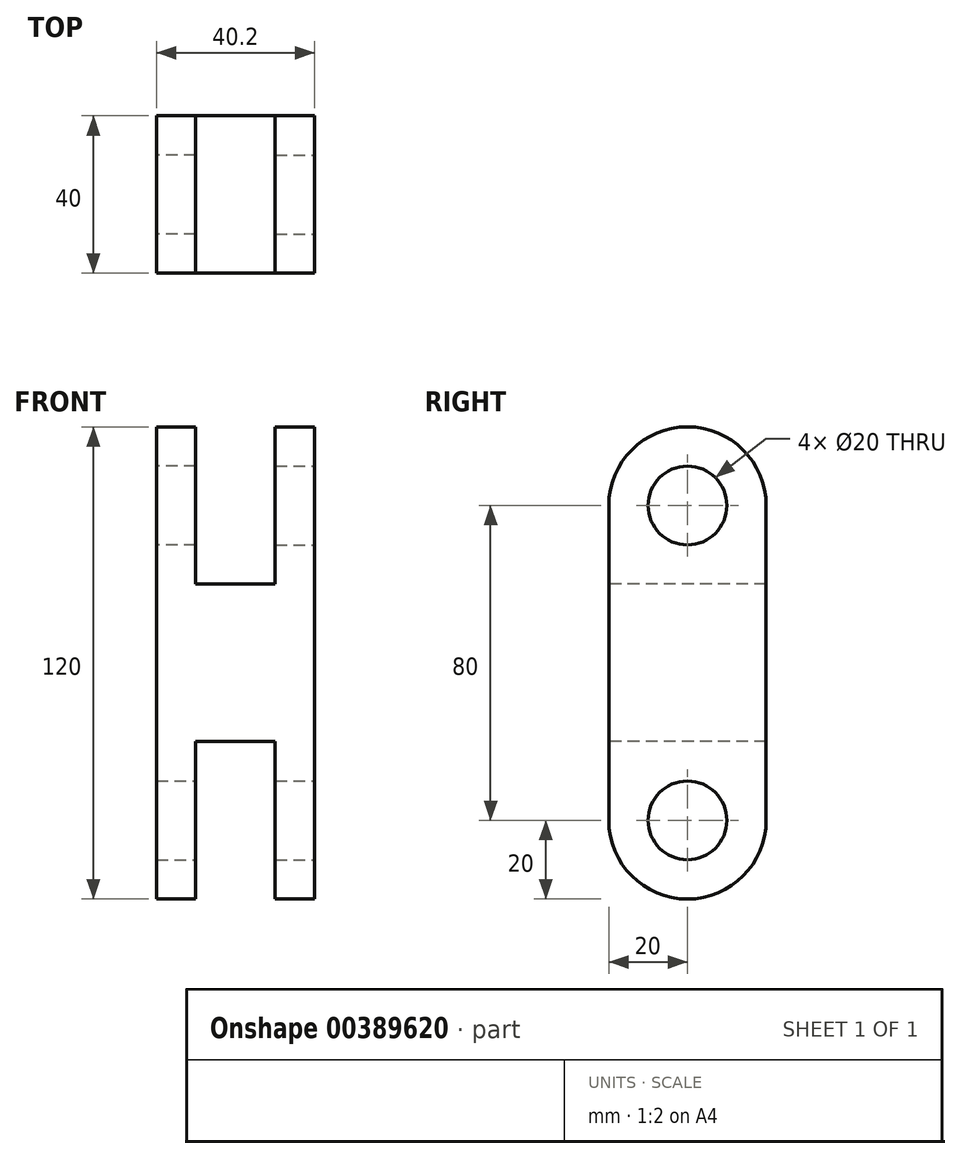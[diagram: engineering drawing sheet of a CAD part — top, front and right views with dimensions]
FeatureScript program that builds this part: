
annotation { "Feature Type Name" : "Feature", "Feature Type Description" : "" }
export const myFeature = defineFeature(function(context is Context, id is Id, definition is map)
    precondition{}
    {
        {
            var Q0;
            Q0=qCreatedBy(makeId("Right.planeOp"),FACE);
            var sketch = newSketch(context, id + "F0", { "sketchPlane" : qUnion([Q0])});
            skLineSegment(sketch, "E0.bottom", {"start": v(20, 40) * mm, "end": v(-20, 40) * mm});
            skLineSegment(sketch, "E0.top", {"start": v(20, -40) * mm, "end": v(-20, -40) * mm});
            skLineSegment(sketch, "E0.left", {"start": v(20, 40) * mm, "end": v(20, -40) * mm});
            skLineSegment(sketch, "E0.right", {"start": v(-20, 40) * mm, "end": v(-20, -40) * mm});
            skPoint(sketch, "E0.middle", {"position": v(0, 0) * mm});
            skSolve(sketch);
        }
        {
            var Q0;
            Q0 = qSketchRegion(id + "F0", true);
            extrude(context, id + "F1", {"entities" : qUnion([Q0]), "depth" : 20.1 * mm});
        }
        {
            var Q0;
            Q0=makeQuery(id+"F1.opExtrude","CAP_FACE",FACE,{"disambiguationData":[OSD([sQuery(id+"F0.wireOp",EDGE,"E0.bottom"),sQuery(id+"F0.wireOp",EDGE,"E0.top"),sQuery(id+"F0.wireOp",EDGE,"E0.left"),sQuery(id+"F0.wireOp",EDGE,"E0.right")])],"isStart":false});
            var sketch = newSketch(context, id + "F2", { "sketchPlane" : qUnion([Q0])});
            skSolve(sketch);
        }
        {
            var Q0;
            Q0=makeQuery(id+"F2.imprint","IMPRINT",FACE,{"disambiguationData":[TD([[makeQuery(id+"F2.imprint","IMPRINT",EDGE,{"derivedFrom":makeQuery(id+"F1.opExtrude","CAP_EDGE",EDGE,{"disambiguationData":[OSD([sQuery(id+"F0.wireOp",EDGE,"E0.bottom")])],"isStart":false})}),1.0]])]});
            var sketch = newSketch(context, id + "F3", { "sketchPlane" : qUnion([Q0])});
            skLineSegment(sketch, "E1.bottom", {"start": v(-20, 40) * mm, "end": v(20, 40) * mm});
            skLineSegment(sketch, "E1.left", {"start": v(-20, 40) * mm, "end": v(-20, 60) * mm});
            skLineSegment(sketch, "E1.right", {"start": v(20, 40) * mm, "end": v(20, 60) * mm});
            skArc(sketch, "E2", {"start": v(20, 60) * mm, "mid": v(0, 80) * mm, "end": v(-20, 60) * mm});
            skCircle(sketch, "E3", {"center": v(0, 60) * mm, "radius": 10 * mm});
            skSolve(sketch);
        }
        {
            var Q0;
            Q0 = qSketchRegion(id + "F3", true);
            extrude(context, id + "F4", {"entities" : qUnion([Q0]), "operationType" : NewBodyOperationType.ADD, "oppositeDirection" : true, "depth" : 10 * mm});
        }
        {
            var Q0;
            Q0=makeQuery(id+"F1.opExtrude","SWEPT_BODY",BODY,{"disambiguationData":[OSD([sQuery(id+"F0.wireOp",EDGE,"E0.bottom"),sQuery(id+"F0.wireOp",EDGE,"E0.top"),sQuery(id+"F0.wireOp",EDGE,"E0.left"),sQuery(id+"F0.wireOp",EDGE,"E0.right")])]});
            var Q1;
            Q1=qCreatedBy(makeId("Right.planeOp"),FACE);
            mirror(context, id + "F5", {"operationType" : NewBodyOperationType.ADD, "entities" : qUnion([Q0]), "mirrorPlane" : qUnion([Q1])});
        }
        {
            var Q0;
            {var subQ0=makeQuery(id+"F4.boolean.opBoolean","MERGE",FACE,{"derivedFrom":[makeQuery(id+"F1.opExtrude","SWEPT_FACE",FACE,{"disambiguationData":[OSD([sQuery(id+"F0.wireOp",EDGE,"E0.right")])]}),makeQuery(id+"F4.opExtrude","SWEPT_FACE",FACE,{"disambiguationData":[OSD([sQuery(id+"F3.wireOp",EDGE,"E1.left")])]})]});Q0=makeQuery(id+"F5.boolean.opBoolean","MERGE",FACE,{"derivedFrom":[subQ0,makeQuery(id+"F5.opPattern","COPY",FACE,{"derivedFrom":subQ0,"instanceName":"1"})]});}
            var sketch = newSketch(context, id + "F6", { "sketchPlane" : qUnion([Q0])});
            skLineSegment(sketch, "E4.bottom", {"start": v(-10.1, -40) * mm, "end": v(10.1, -40) * mm});
            skLineSegment(sketch, "E4.top", {"start": v(-10.1, 0) * mm, "end": v(10.1, 0) * mm});
            skLineSegment(sketch, "E4.left", {"start": v(-10.1, -40) * mm, "end": v(-10.1, 0) * mm});
            skLineSegment(sketch, "E4.right", {"start": v(10.1, -40) * mm, "end": v(10.1, 0) * mm});
            skSolve(sketch);
        }
        {
            var Q0;
            Q0 = qSketchRegion(id + "F6", true);
            var Q1;
            {var subQ0=makeQuery(id+"F4.boolean.opBoolean","MERGE",FACE,{"derivedFrom":[makeQuery(id+"F1.opExtrude","SWEPT_FACE",FACE,{"disambiguationData":[OSD([sQuery(id+"F0.wireOp",EDGE,"E0.left")])]}),makeQuery(id+"F4.opExtrude","SWEPT_FACE",FACE,{"disambiguationData":[OSD([sQuery(id+"F3.wireOp",EDGE,"E1.right")])]})]});Q1=makeQuery(id+"F5.boolean.opBoolean","MERGE",FACE,{"derivedFrom":[subQ0,makeQuery(id+"F5.opPattern","COPY",FACE,{"derivedFrom":subQ0,"instanceName":"1"})]});}
            extrude(context, id + "F7", {"entities" : qUnion([Q0]), "operationType" : NewBodyOperationType.REMOVE, "endBound" : BoundingType.UP_TO_SURFACE, "oppositeDirection" : true, "endBoundEntityFace" : qUnion([Q1]), "depth" : 25 * mm});
        }
        {
            var Q0;
            Q0=makeQuery(id+"F2.imprint","IMPRINT",FACE,{"disambiguationData":[TD([[makeQuery(id+"F2.imprint","IMPRINT",EDGE,{"derivedFrom":makeQuery(id+"F1.opExtrude","CAP_EDGE",EDGE,{"disambiguationData":[OSD([sQuery(id+"F0.wireOp",EDGE,"E0.bottom")])],"isStart":false})}),1.0]])]});
            var sketch = newSketch(context, id + "F8", { "sketchPlane" : qUnion([Q0])});
            skLineSegment(sketch, "E5", {"start": v(0, -40) * mm, "end": v(0, -20) * mm, "construction": true});
            skCircle(sketch, "E6", {"center": v(0, -20) * mm, "radius": 10 * mm});
            skSolve(sketch);
        }
        {
            var Q0;
            Q0 = qSketchRegion(id + "F8", true);
            var Q1;
            Q1=makeQuery(id+"F5.opPattern","COPY",FACE,{"derivedFrom":makeQuery(id+"F4.boolean.opBoolean","MERGE",FACE,{"derivedFrom":[makeQuery(id+"F1.opExtrude","CAP_FACE",FACE,{"disambiguationData":[OSD([sQuery(id+"F0.wireOp",EDGE,"E0.bottom"),sQuery(id+"F0.wireOp",EDGE,"E0.top"),sQuery(id+"F0.wireOp",EDGE,"E0.left"),sQuery(id+"F0.wireOp",EDGE,"E0.right")])],"isStart":false}),makeQuery(id+"F4.opExtrude","CAP_FACE",FACE,{"disambiguationData":[OSD([sQuery(id+"F3.wireOp",EDGE,"E1.bottom"),sQuery(id+"F3.wireOp",EDGE,"E1.left"),sQuery(id+"F3.wireOp",EDGE,"E1.right"),sQuery(id+"F3.wireOp",EDGE,"E2"),sQuery(id+"F3.wireOp",EDGE,"E3")])],"isStart":true})]}),"instanceName":"1"});
            extrude(context, id + "F9", {"entities" : qUnion([Q0]), "operationType" : NewBodyOperationType.REMOVE, "endBound" : BoundingType.UP_TO_SURFACE, "oppositeDirection" : true, "endBoundEntityFace" : qUnion([Q1]), "depth" : 25 * mm});
        }
        {
            var Q0;
            {var subQ1=sQuery(id+"F0.wireOp",EDGE,"E0.right");var subQ3=sQuery(id+"F0.wireOp",EDGE,"E0.top");var subQ6=makeQuery(id+"F1.opExtrude","SWEPT_EDGE",EDGE,{"disambiguationData":[OSD([subQ3,subQ1])]});Q0=makeQuery(id+"F7.boolean.opBoolean","SPLIT",EDGE,{"disambiguationData":[TD([makeQuery(id+"F7.opExtrude","SWEPT_FACE",FACE,{"disambiguationData":[OSD([sQuery(id+"F6.wireOp",EDGE,"E4.right")])]})])],"derivedFrom":makeQuery(id+"F5.boolean.opBoolean","MERGE",EDGE,{"derivedFrom":[subQ6,makeQuery(id+"F5.opPattern","COPY",EDGE,{"derivedFrom":subQ6,"instanceName":"1"})]})});}
            var Q1;
            {var subQ0=sQuery(id+"F0.wireOp",EDGE,"E0.right");var subQ2=sQuery(id+"F0.wireOp",EDGE,"E0.top");var subQ6=makeQuery(id+"F1.opExtrude","SWEPT_EDGE",EDGE,{"disambiguationData":[OSD([subQ2,subQ0])]});Q1=makeQuery(id+"F7.boolean.opBoolean","SPLIT",EDGE,{"disambiguationData":[TD([makeQuery(id+"F7.opExtrude","SWEPT_FACE",FACE,{"disambiguationData":[OSD([sQuery(id+"F6.wireOp",EDGE,"E4.left")])]})])],"derivedFrom":makeQuery(id+"F5.boolean.opBoolean","MERGE",EDGE,{"derivedFrom":[subQ6,makeQuery(id+"F5.opPattern","COPY",EDGE,{"derivedFrom":subQ6,"instanceName":"1"})]})});}
            var Q2;
            {var subQ2=sQuery(id+"F0.wireOp",EDGE,"E0.left");var subQ4=sQuery(id+"F0.wireOp",EDGE,"E0.top");var subQ6=makeQuery(id+"F1.opExtrude","SWEPT_EDGE",EDGE,{"disambiguationData":[OSD([subQ4,subQ2])]});Q2=makeQuery(id+"F7.boolean.opBoolean","SPLIT",EDGE,{"disambiguationData":[TD([makeQuery(id+"F7.opExtrude","SWEPT_FACE",FACE,{"disambiguationData":[OSD([sQuery(id+"F6.wireOp",EDGE,"E4.left")])]})])],"derivedFrom":makeQuery(id+"F5.boolean.opBoolean","MERGE",EDGE,{"derivedFrom":[subQ6,makeQuery(id+"F5.opPattern","COPY",EDGE,{"derivedFrom":subQ6,"instanceName":"1"})]})});}
            var Q3;
            {var subQ1=sQuery(id+"F0.wireOp",EDGE,"E0.left");var subQ3=sQuery(id+"F0.wireOp",EDGE,"E0.top");var subQ6=makeQuery(id+"F1.opExtrude","SWEPT_EDGE",EDGE,{"disambiguationData":[OSD([subQ3,subQ1])]});Q3=makeQuery(id+"F7.boolean.opBoolean","SPLIT",EDGE,{"disambiguationData":[TD([makeQuery(id+"F7.opExtrude","SWEPT_FACE",FACE,{"disambiguationData":[OSD([sQuery(id+"F6.wireOp",EDGE,"E4.right")])]})])],"derivedFrom":makeQuery(id+"F5.boolean.opBoolean","MERGE",EDGE,{"derivedFrom":[subQ6,makeQuery(id+"F5.opPattern","COPY",EDGE,{"derivedFrom":subQ6,"instanceName":"1"})]})});}
            fillet(context, id + "F10", {"entities" : qUnion([Q0, Q1, Q2, Q3]), "radius" : 20 * mm, "tangentPropagation" : true, "allowEdgeOverflow" : false});
        }
    });
